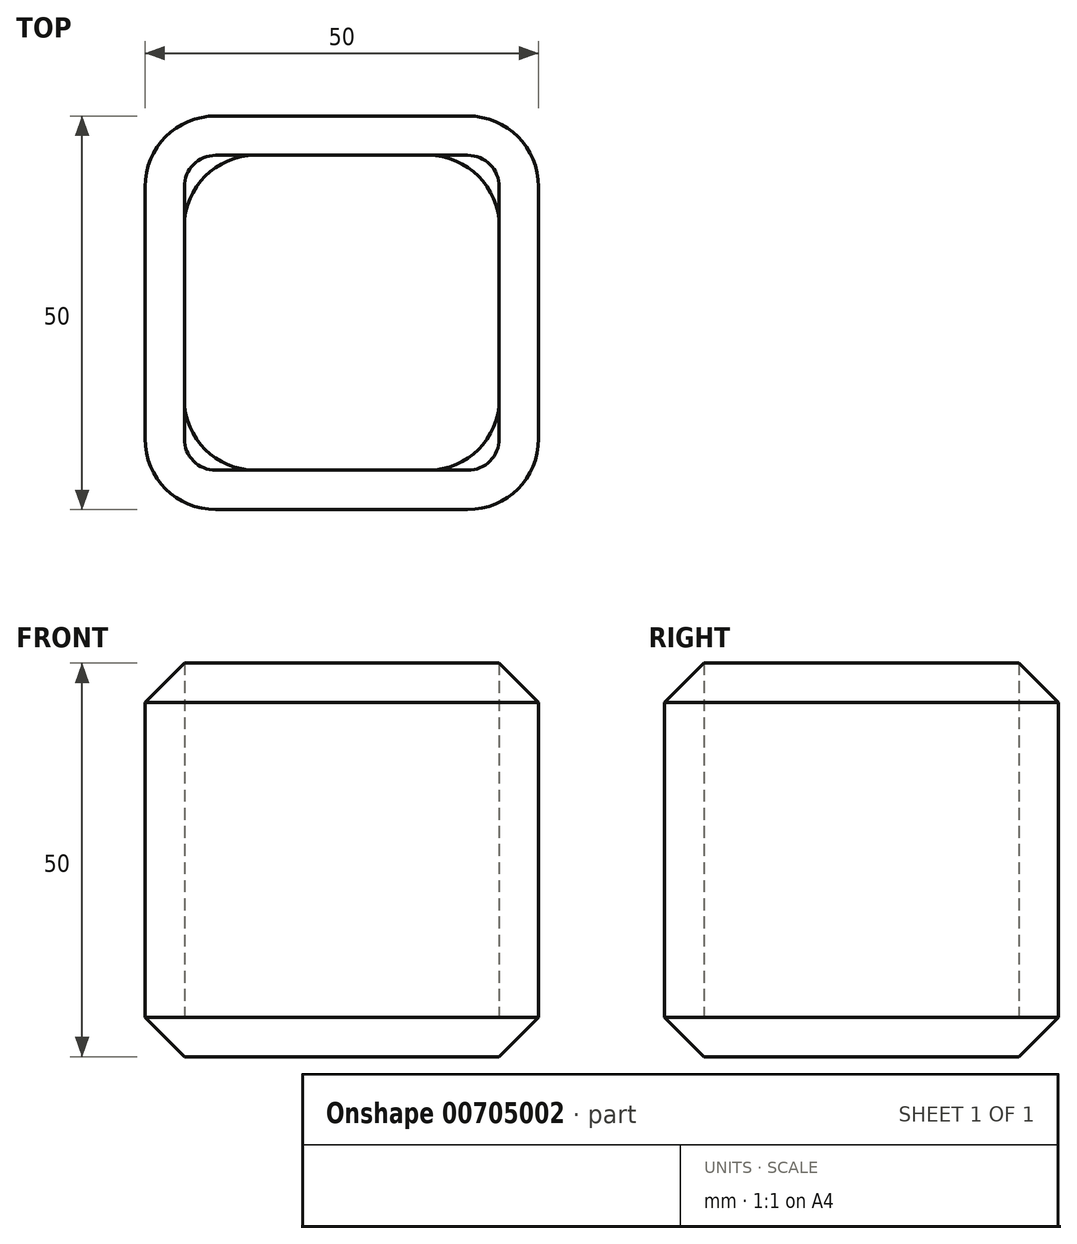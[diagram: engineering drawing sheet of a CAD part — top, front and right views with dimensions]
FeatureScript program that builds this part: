
annotation { "Feature Type Name" : "Feature", "Feature Type Description" : "" }
export const myFeature = defineFeature(function(context is Context, id is Id, definition is map)
    precondition{}
    {
        {
            var Q0;
            Q0=qCreatedBy(makeId("Top.planeOp"),FACE);
            var sketch = newSketch(context, id + "F0", { "sketchPlane" : qUnion([Q0])});
            skLineSegment(sketch, "E0.bottom", {"start": v(25, -25) * mm, "end": v(-25, -25) * mm});
            skLineSegment(sketch, "E0.top", {"start": v(25, 25) * mm, "end": v(-25, 25) * mm});
            skLineSegment(sketch, "E0.left", {"start": v(25, -25) * mm, "end": v(25, 25) * mm});
            skLineSegment(sketch, "E0.right", {"start": v(-25, -25) * mm, "end": v(-25, 25) * mm});
            skPoint(sketch, "E0.middle", {"position": v(0, 0) * mm});
            skSolve(sketch);
        }
        {
            var Q0;
            Q0 = qSketchRegion(id + "F0", true);
            extrude(context, id + "F1", {"entities" : qUnion([Q0]), "depth" : 50 * mm, "offsetDistance" : 25.4 * mm});
        }
        {
            var Q0;
            Q0=makeQuery(id+"F1.opExtrude","CAP_FACE",FACE,{"disambiguationData":[OSD([sQuery(id+"F0.wireOp",EDGE,"E0.bottom"),sQuery(id+"F0.wireOp",EDGE,"E0.top"),sQuery(id+"F0.wireOp",EDGE,"E0.left"),sQuery(id+"F0.wireOp",EDGE,"E0.right")])],"isStart":false});
            shell(context, id + "F2", {"entities" : qUnion([Q0]), "thickness" : 5 * mm});
        }
        {
            var Q0;
            Q0=makeQuery(id+"F1.opExtrude","SWEPT_EDGE",EDGE,{"disambiguationData":[OSD([sQuery(id+"F0.wireOp",EDGE,"E0.top"),sQuery(id+"F0.wireOp",EDGE,"E0.right")])]});
            var Q1;
            Q1=makeQuery(id+"F1.opExtrude","SWEPT_EDGE",EDGE,{"disambiguationData":[OSD([sQuery(id+"F0.wireOp",EDGE,"E0.bottom"),sQuery(id+"F0.wireOp",EDGE,"E0.right")])]});
            var Q2;
            Q2=makeQuery(id+"F1.opExtrude","SWEPT_EDGE",EDGE,{"disambiguationData":[OSD([sQuery(id+"F0.wireOp",EDGE,"E0.bottom"),sQuery(id+"F0.wireOp",EDGE,"E0.left")])]});
            var Q3;
            Q3=makeQuery(id+"F1.opExtrude","SWEPT_EDGE",EDGE,{"disambiguationData":[OSD([sQuery(id+"F0.wireOp",EDGE,"E0.top"),sQuery(id+"F0.wireOp",EDGE,"E0.left")])]});
            var Q4;
            Q4=makeQuery(id+"F2.opShell","OFFSET_EDGE",EDGE,{"disambiguationData":[OSD([sQuery(id+"F0.wireOp",EDGE,"E0.bottom"),sQuery(id+"F0.wireOp",EDGE,"E0.left")])]});
            var Q5;
            Q5=makeQuery(id+"F2.opShell","OFFSET_EDGE",EDGE,{"disambiguationData":[OSD([sQuery(id+"F0.wireOp",EDGE,"E0.bottom"),sQuery(id+"F0.wireOp",EDGE,"E0.right")])]});
            var Q6;
            Q6=makeQuery(id+"F2.opShell","OFFSET_EDGE",EDGE,{"disambiguationData":[OSD([sQuery(id+"F0.wireOp",EDGE,"E0.top"),sQuery(id+"F0.wireOp",EDGE,"E0.right")])]});
            var Q7;
            Q7=makeQuery(id+"F2.opShell","OFFSET_EDGE",EDGE,{"disambiguationData":[OSD([sQuery(id+"F0.wireOp",EDGE,"E0.top"),sQuery(id+"F0.wireOp",EDGE,"E0.left")])]});
            fillet(context, id + "F3", {"entities" : qUnion([Q0, Q1, Q2, Q3, Q4, Q5, Q6, Q7]), "radius" : 9 * mm, "tangentPropagation" : true, "allowEdgeOverflow" : false});
        }
        {
            var Q0;
            Q0=makeQuery(id+"F1.opExtrude","SWEPT_FACE",FACE,{"disambiguationData":[OSD([sQuery(id+"F0.wireOp",EDGE,"E0.left")])]});
            var Q1;
            Q1=makeQuery(id+"F1.opExtrude","SWEPT_FACE",FACE,{"disambiguationData":[OSD([sQuery(id+"F0.wireOp",EDGE,"E0.top")])]});
            var Q2;
            Q2=makeQuery(id+"F1.opExtrude","SWEPT_FACE",FACE,{"disambiguationData":[OSD([sQuery(id+"F0.wireOp",EDGE,"E0.right")])]});
            var Q3;
            Q3=makeQuery(id+"F1.opExtrude","SWEPT_FACE",FACE,{"disambiguationData":[OSD([sQuery(id+"F0.wireOp",EDGE,"E0.bottom")])]});
            chamfer(context, id + "F4", {"entities" : qUnion([Q0, Q1, Q2, Q3]), "width" : 5 * mm, "tangentPropagation" : true});
        }
    });
